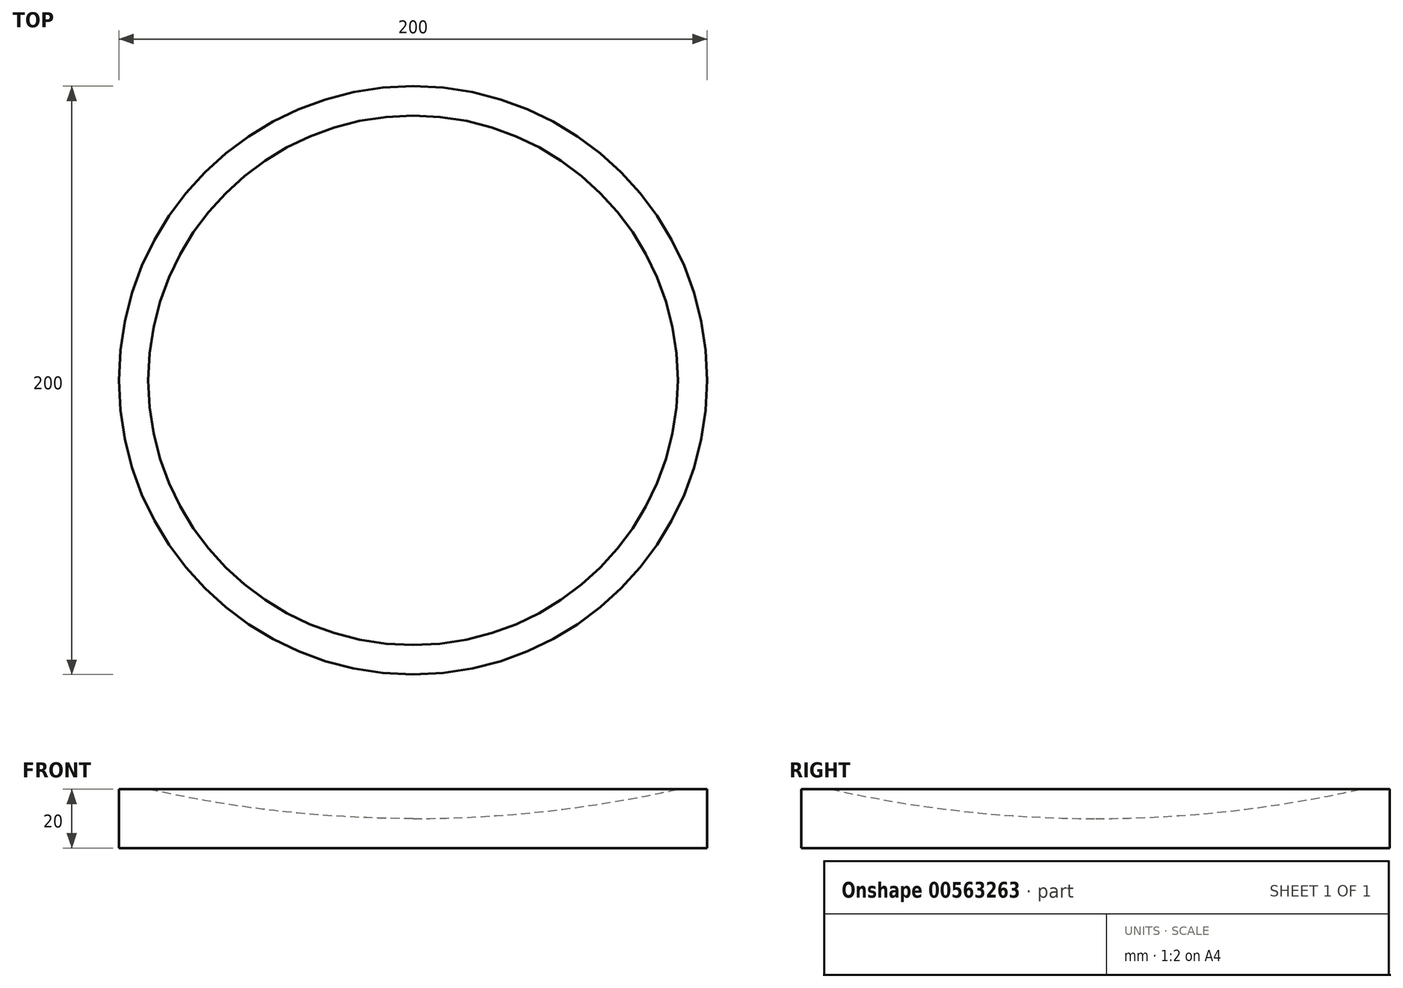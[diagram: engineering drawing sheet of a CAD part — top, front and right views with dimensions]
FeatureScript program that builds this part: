
annotation { "Feature Type Name" : "Feature", "Feature Type Description" : "" }
export const myFeature = defineFeature(function(context is Context, id is Id, definition is map)
    precondition{}
    {
        {
            var Q0;
            Q0=qCreatedBy(makeId("Front.planeOp"),FACE);
            var sketch = newSketch(context, id + "F0", { "sketchPlane" : qUnion([Q0])});
            skLineSegment(sketch, "E0", {"start": v(0, 0) * mm, "end": v(-100, 0) * mm});
            skLineSegment(sketch, "E1", {"start": v(-100, 0) * mm, "end": v(-100, 20) * mm});
            skLineSegment(sketch, "E2", {"start": v(-100, 20) * mm, "end": v(-90, 20) * mm});
            skArc(sketch, "E3", {"start": v(-90, 20) * mm, "mid": v(-45.28, 12.5) * mm, "end": v(0, 10) * mm});
            skLineSegment(sketch, "E4", {"start": v(0, 10) * mm, "end": v(0, 0) * mm});
            skSolve(sketch);
        }
        {
            var Q0;
            Q0=makeQuery(id+"F0.imprint","IMPRINT",FACE,{"disambiguationData":[TD([[makeQuery(id+"F0.imprint","IMPRINT",EDGE,{"derivedFrom":sQuery(id+"F0.wireOp",EDGE,"E0")}),-1.0]])]});
            var Q1;
            Q1=sQuery(id+"F0.wireOp",EDGE,"E4");
            revolve(context, id + "F1", {"entities" : qUnion([Q0]), "axis" : qUnion([Q1]), "revolveType" : RevolveType.FULL});
        }
    });
